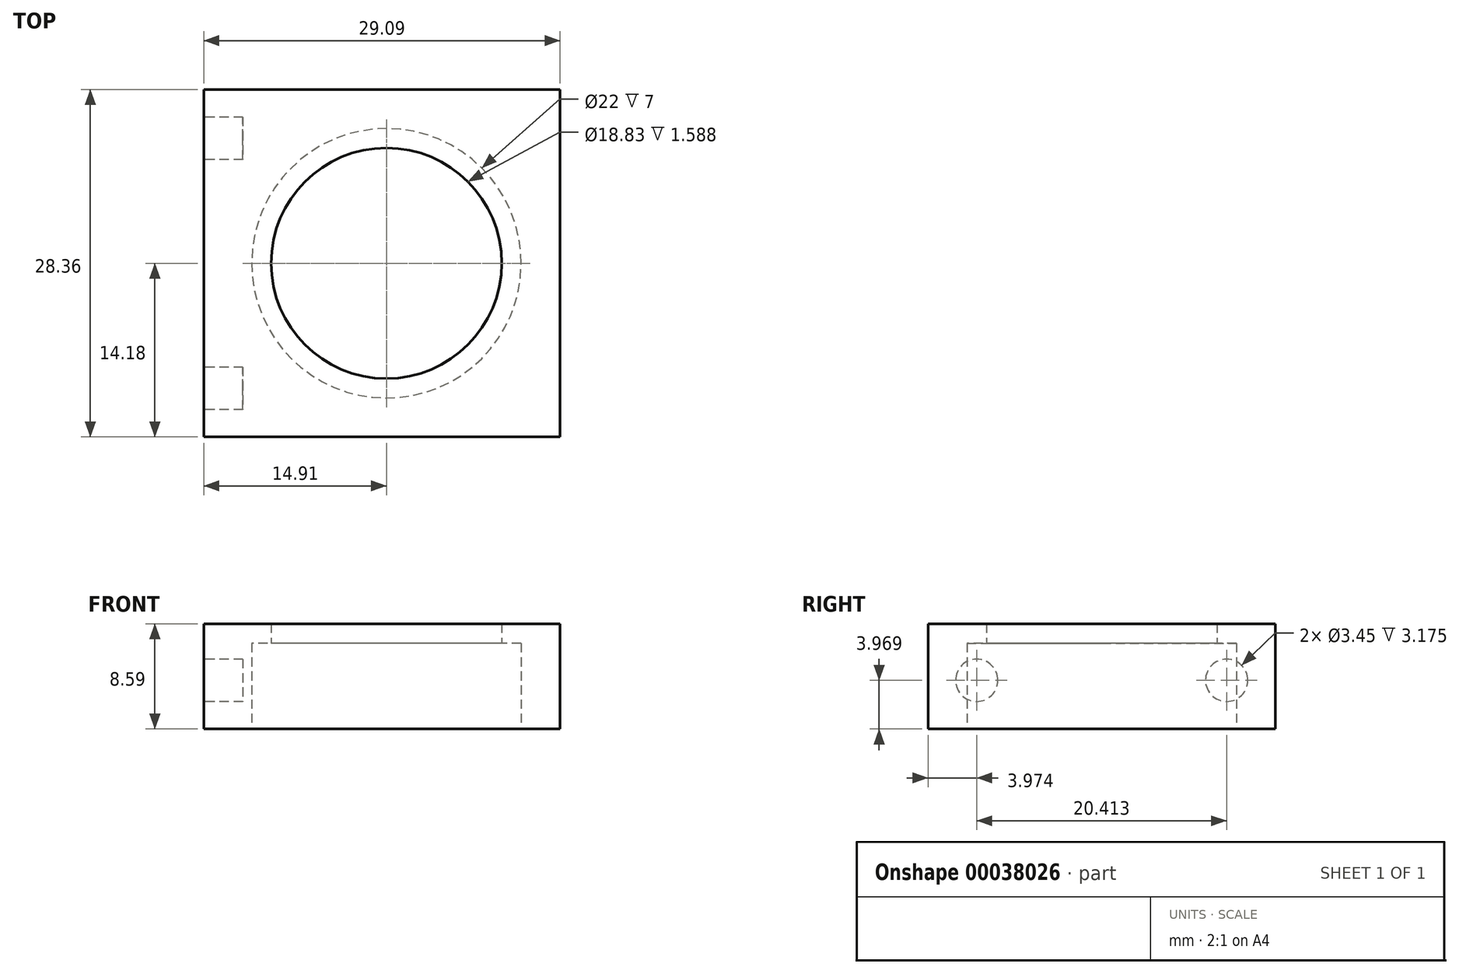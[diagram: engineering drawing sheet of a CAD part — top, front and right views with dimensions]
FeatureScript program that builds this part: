
annotation { "Feature Type Name" : "Feature", "Feature Type Description" : "" }
export const myFeature = defineFeature(function(context is Context, id is Id, definition is map)
    precondition{}
    {
        {
            var Q0;
            Q0=qCreatedBy(makeId("Top.planeOp"),FACE);
            var sketch = newSketch(context, id + "F0", { "sketchPlane" : qUnion([Q0])});
            skCircle(sketch, "E0", {"center": v(0, 0) * mm, "radius": 11 * mm});
            skLineSegment(sketch, "E1", {"start": v(0, 14.18) * mm, "end": v(0, -14.18) * mm, "construction": true});
            skLineSegment(sketch, "E2", {"start": v(0, 14.18) * mm, "end": v(-14.9, 14.18) * mm});
            skLineSegment(sketch, "E3", {"start": v(-14.9, 14.18) * mm, "end": v(-14.9, -14.18) * mm});
            skLineSegment(sketch, "E4", {"start": v(-14.9, -14.18) * mm, "end": v(0, -14.18) * mm});
            skLineSegment(sketch, "E5.bottom", {"start": v(14.18, -14.18) * mm, "end": v(0, -14.18) * mm});
            skLineSegment(sketch, "E5.top", {"start": v(14.18, 14.18) * mm, "end": v(0, 14.18) * mm});
            skLineSegment(sketch, "E5.left", {"start": v(14.18, -14.18) * mm, "end": v(14.18, 14.18) * mm});
            skArc(sketch, "E6", {"start": v(0, -14.18) * mm, "mid": v(14.18, 0) * mm, "end": v(0, 14.18) * mm, "construction": true});
            skLineSegment(sketch, "E7.rect.bottom", {"start": v(-14.9, 7.96) * mm, "end": v(-11.73, 7.96) * mm, "construction": true});
            skLineSegment(sketch, "E7.rect.top", {"start": v(-14.9, 12.45) * mm, "end": v(-11.73, 12.45) * mm, "construction": true});
            skLineSegment(sketch, "E7.rect.right", {"start": v(-11.73, 7.96) * mm, "end": v(-11.73, 12.45) * mm, "construction": true});
            skPoint(sketch, "E7.rect.middle", {"position": v(-13.32, 10.2) * mm});
            skArc(sketch, "E8", {"start": v(0, 14.18) * mm, "mid": v(-14.18, 0) * mm, "end": v(0, -14.18) * mm, "construction": true});
            skLineSegment(sketch, "E9", {"start": v(-13.32, 10.2) * mm, "end": v(-13.32, 14.18) * mm, "construction": true});
            skSolve(sketch);
        }
        {
            var Q0;
            Q0=qSketchRegion(id+"F0",true);
            extrude(context, id + "F1", {"entities" : qUnion([Q0]), "depth" : 7 * mm});
        }
        {
            var Q0;
            Q0=makeQuery(id+"F1.opExtrude","CAP_FACE",FACE,{"disambiguationData":[OSD([sQuery(id+"F0.wireOp",EDGE,"E0"),sQuery(id+"F0.wireOp",EDGE,"4360b9c9-94da-410b-b3ec-ac22ef273fc6"),sQuery(id+"F0.wireOp",EDGE,"E2"),sQuery(id+"F0.wireOp",EDGE,"E3"),sQuery(id+"F0.wireOp",EDGE,"E4"),sQuery(id+"F0.wireOp",EDGE,"5ffc639e-95c1-44d1-9af8-e9582f762f33"),sQuery(id+"F0.wireOp",EDGE,"6ae625d0-022c-4fec-8211-c5fa541366f6")])],"isStart":false});
            var sketch = newSketch(context, id + "F2", { "sketchPlane" : qUnion([Q0])});
            skCircle(sketch, "E10", {"center": v(0, 0) * mm, "radius": 9.41 * mm});
            skSolve(sketch);
        }
        {
            var Q0;
            Q0=makeQuery(id+"F2.imprint","IMPRINT",FACE,{"disambiguationData":[TD([[makeQuery(id+"F2.imprint","IMPRINT",EDGE,{"derivedFrom":sQuery(id+"F2.wireOp",EDGE,"E10")}),-1.0]])]});
            var Q1;
            Q1=makeQuery(id+"F2.imprint","IMPRINT",FACE,{"disambiguationData":[TD([[makeQuery(id+"F2.imprint","IMPRINT",EDGE,{"derivedFrom":makeQuery(id+"F1.opExtrude","CAP_EDGE",EDGE,{"disambiguationData":[OSD([sQuery(id+"F0.wireOp",EDGE,"E0")])],"isStart":false})}),-1.0]])]});
            extrude(context, id + "F3", {"entities" : qUnion([Q0, Q1]), "operationType" : NewBodyOperationType.ADD, "depth" : 1.59 * mm});
        }
        {
            var Q0;
            {var subQ0=sQuery(id+"F0.wireOp",EDGE,"E3");Q0=makeQuery(id+"F3.boolean.opBoolean","MERGE",FACE,{"derivedFrom":[makeQuery(id+"F1.opExtrude","SWEPT_FACE",FACE,{"disambiguationData":[OSD([subQ0])]}),makeQuery(id+"F3.opExtrude","SWEPT_FACE",FACE,{"disambiguationData":[OSD([subQ0])]})]});}
            var sketch = newSketch(context, id + "F4", { "sketchPlane" : qUnion([Q0])});
            skCircle(sketch, "E11", {"center": v(10.2, 3.97) * mm, "radius": 1.73 * mm});
            skCircle(sketch, "E12", {"center": v(-10.2, 3.97) * mm, "radius": 1.73 * mm});
            skLineSegment(sketch, "E13.bottom", {"start": v(14.18, 0) * mm, "end": v(10.2, 0) * mm, "construction": true});
            skLineSegment(sketch, "E13.top", {"start": v(14.18, 3.97) * mm, "end": v(10.2, 3.97) * mm, "construction": true});
            skLineSegment(sketch, "E13.left", {"start": v(14.18, 0) * mm, "end": v(14.18, 3.97) * mm, "construction": true});
            skLineSegment(sketch, "E13.right", {"start": v(10.2, 0) * mm, "end": v(10.2, 3.97) * mm, "construction": true});
            skLineSegment(sketch, "E14.bottom", {"start": v(-14.18, 0) * mm, "end": v(-10.2, 0) * mm, "construction": true});
            skLineSegment(sketch, "E14.top", {"start": v(-14.18, 3.97) * mm, "end": v(-10.2, 3.97) * mm, "construction": true});
            skLineSegment(sketch, "E14.left", {"start": v(-14.18, 0) * mm, "end": v(-14.18, 3.97) * mm, "construction": true});
            skLineSegment(sketch, "E14.right", {"start": v(-10.2, 0) * mm, "end": v(-10.2, 3.97) * mm, "construction": true});
            skSolve(sketch);
        }
        {
            var Q0;
            Q0 = qSketchRegion(id + "F4", true);
            extrude(context, id + "F5", {"entities" : qUnion([Q0]), "operationType" : NewBodyOperationType.REMOVE, "oppositeDirection" : true, "depth" : 3.17 * mm});
        }
    });
